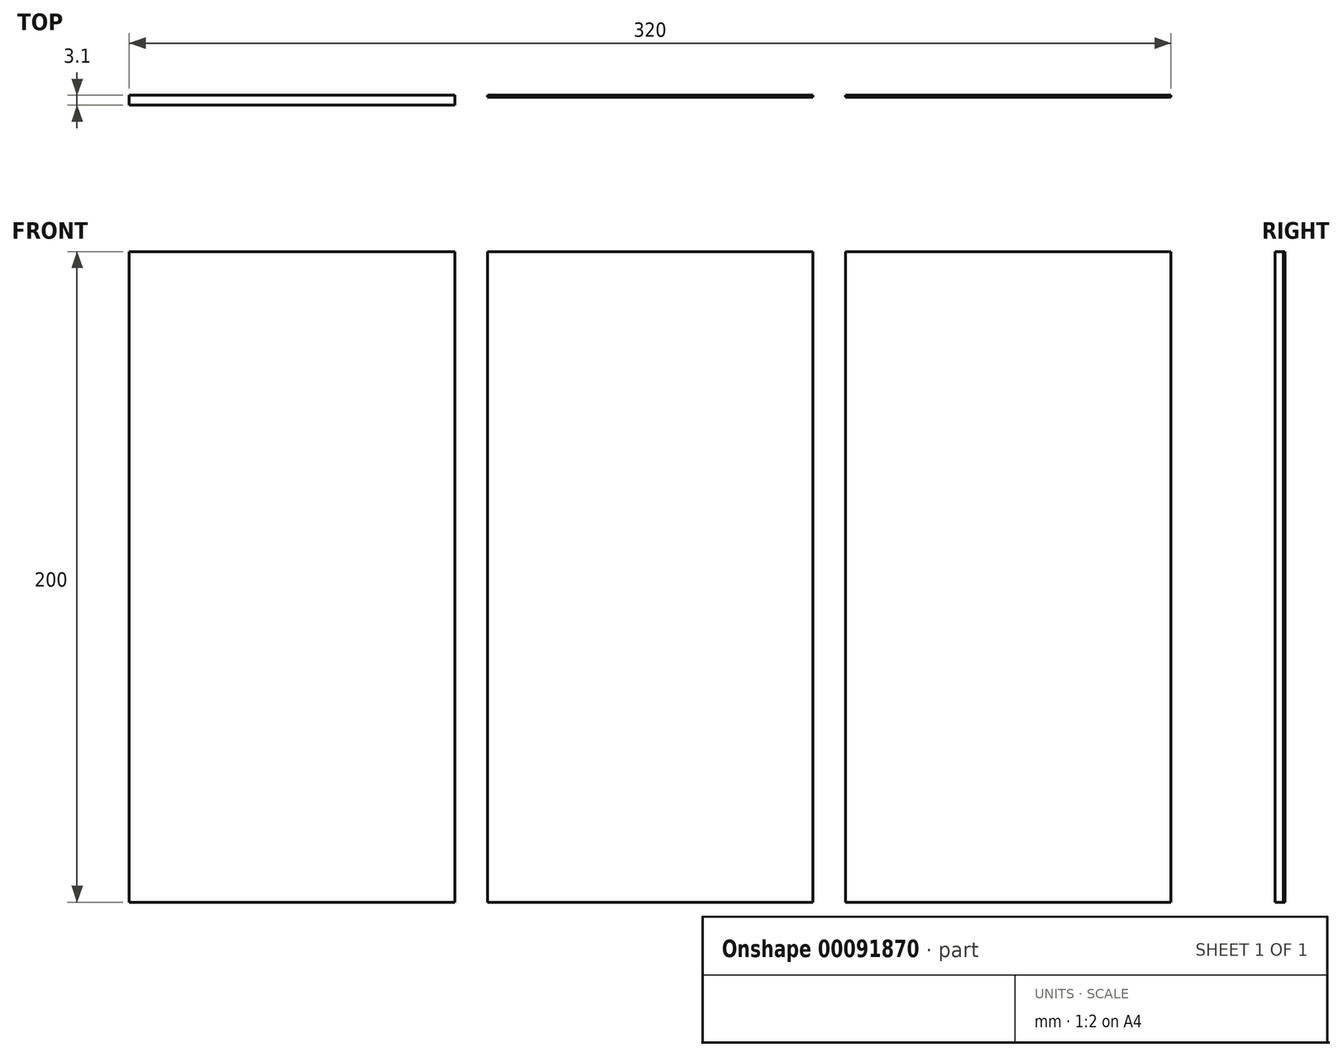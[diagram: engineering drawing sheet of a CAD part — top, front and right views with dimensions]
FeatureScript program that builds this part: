
annotation { "Feature Type Name" : "Feature", "Feature Type Description" : "" }
export const myFeature = defineFeature(function(context is Context, id is Id, definition is map)
    precondition{}
    {
        {
            var Q0;
            Q0=qCreatedBy(makeId("Front.planeOp"),FACE);
            var sketch = newSketch(context, id + "F0", { "sketchPlane" : qUnion([Q0])});
            skLineSegment(sketch, "E0.bottom", {"start": v(-50, 100) * mm, "end": v(50, 100) * mm});
            skLineSegment(sketch, "E0.top", {"start": v(-50, -100) * mm, "end": v(50, -100) * mm});
            skLineSegment(sketch, "E0.left", {"start": v(-50, 100) * mm, "end": v(-50, -100) * mm});
            skLineSegment(sketch, "E0.right", {"start": v(50, 100) * mm, "end": v(50, -100) * mm});
            skPoint(sketch, "E0.middle", {"position": v(0, 0) * mm});
            skSolve(sketch);
        }
        {
            var Q0;
            Q0=makeQuery(id+"F0.imprint","IMPRINT",FACE,{"disambiguationData":[TD([[makeQuery(id+"F0.imprint","IMPRINT",EDGE,{"derivedFrom":sQuery(id+"F0.wireOp",EDGE,"E0.bottom")}),-1.0]])]});
            extrude(context, id + "F1", {"entities" : qUnion([Q0]), "depth" : 3 * mm, "symmetric" : true});
        }
        {
            var Q0;
            Q0=makeQuery(id+"F1.opExtrude","CAP_FACE",FACE,{"disambiguationData":[OSD([sQuery(id+"F0.wireOp",EDGE,"E0.bottom"),sQuery(id+"F0.wireOp",EDGE,"E0.top"),sQuery(id+"F0.wireOp",EDGE,"E0.left"),sQuery(id+"F0.wireOp",EDGE,"E0.right")])],"isStart":false});
            var sketch = newSketch(context, id + "F2", { "sketchPlane" : qUnion([Q0])});
            skLineSegment(sketch, "E1.bottom", {"start": v(50, -100) * mm, "end": v(-50, -100) * mm});
            skLineSegment(sketch, "E1.top", {"start": v(50, 100) * mm, "end": v(-50, 100) * mm});
            skLineSegment(sketch, "E1.left", {"start": v(50, -100) * mm, "end": v(50, 100) * mm});
            skLineSegment(sketch, "E1.right", {"start": v(-50, -100) * mm, "end": v(-50, 100) * mm});
            skPoint(sketch, "E1.middle", {"position": v(0, 0) * mm});
            skSolve(sketch);
        }
        {
            var Q0;
            Q0 = qSketchRegion(id + "F2", true);
            extrude(context, id + "F3", {"entities" : qUnion([Q0]), "operationType" : NewBodyOperationType.ADD, "depth" : 0.1 * mm});
        }
        {
            var Q0;
            Q0=makeQuery(id+"F1.opExtrude","SWEPT_BODY",BODY,{"disambiguationData":[OSD([sQuery(id+"F0.wireOp",EDGE,"E0.bottom"),sQuery(id+"F0.wireOp",EDGE,"E0.top"),sQuery(id+"F0.wireOp",EDGE,"E0.left"),sQuery(id+"F0.wireOp",EDGE,"E0.right")])]});
            transform(context, id + "F4", {"entities" : qUnion([Q0]), "transformType" : TransformType.TRANSLATION_3D, "dx" : 110 * mm, "dy" : 0 * mm, "dz" : 0 * mm, "makeCopy" : true});
        }
        {
            var Q0;
            Q0=makeQuery(id+"F4.opPattern","COPY",FACE,{"derivedFrom":makeQuery(id+"F3.opExtrude","CAP_FACE",FACE,{"disambiguationData":[OSD([sQuery(id+"F2.wireOp",EDGE,"E1.bottom"),sQuery(id+"F2.wireOp",EDGE,"E1.top"),sQuery(id+"F2.wireOp",EDGE,"E1.left"),sQuery(id+"F2.wireOp",EDGE,"E1.right")])],"isStart":false}),"instanceName":"1"});
            extrude(context, id + "F5", {"entities" : qUnion([Q0]), "operationType" : NewBodyOperationType.REMOVE, "oppositeDirection" : true, "depth" : 2.5 * mm});
        }
        {
            var Q0;
            Q0=makeQuery(id+"F4.opPattern","COPY",BODY,{"derivedFrom":makeQuery(id+"F1.opExtrude","SWEPT_BODY",BODY,{"disambiguationData":[OSD([sQuery(id+"F0.wireOp",EDGE,"E0.bottom"),sQuery(id+"F0.wireOp",EDGE,"E0.top"),sQuery(id+"F0.wireOp",EDGE,"E0.left"),sQuery(id+"F0.wireOp",EDGE,"E0.right")])]}),"instanceName":"1"});
            transform(context, id + "F6", {"entities" : qUnion([Q0]), "transformType" : TransformType.TRANSLATION_3D, "dx" : 110 * mm, "dy" : 0 * mm, "dz" : 0 * mm, "makeCopy" : true});
        }
    });
